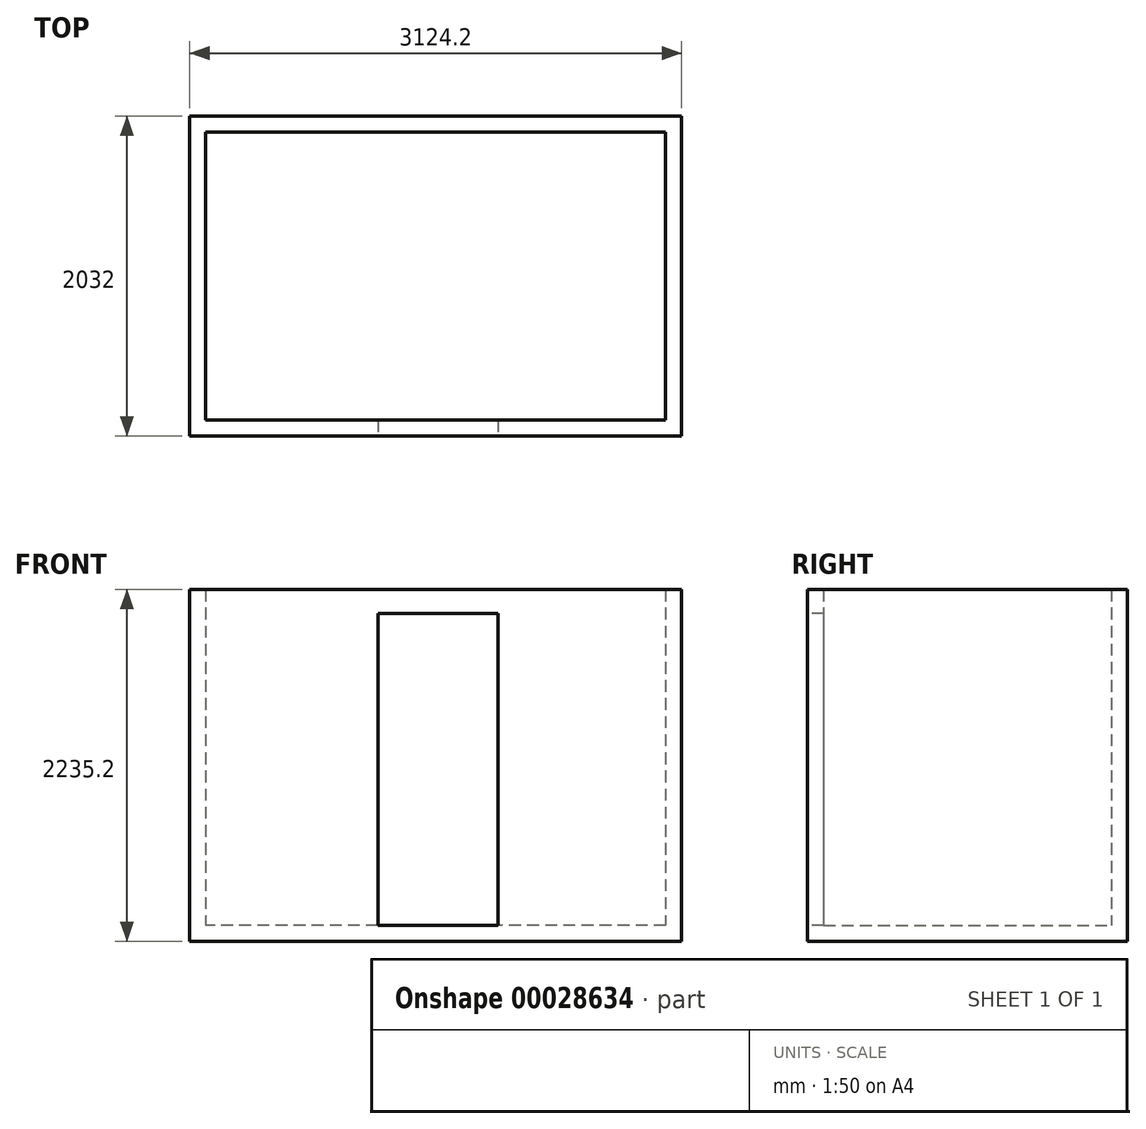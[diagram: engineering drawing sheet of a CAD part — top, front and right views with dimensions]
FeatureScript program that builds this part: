
annotation { "Feature Type Name" : "Feature", "Feature Type Description" : "" }
export const myFeature = defineFeature(function(context is Context, id is Id, definition is map)
    precondition{}
    {
        {
            var Q0;
            Q0=qCreatedBy(makeId("Top.planeOp"),FACE);
            var sketch = newSketch(context, id + "F0", { "sketchPlane" : qUnion([Q0])});
            skLineSegment(sketch, "E0.rect.bottom", {"start": v(1460.5, -914.4) * mm, "end": v(-1460.5, -914.4) * mm});
            skLineSegment(sketch, "E0.rect.top", {"start": v(1460.5, 914.4) * mm, "end": v(-1460.5, 914.4) * mm});
            skLineSegment(sketch, "E0.rect.left", {"start": v(1460.5, -914.4) * mm, "end": v(1460.5, 914.4) * mm});
            skLineSegment(sketch, "E0.rect.right", {"start": v(-1460.5, -914.4) * mm, "end": v(-1460.5, 914.4) * mm});
            skPoint(sketch, "E0.rect.middle", {"position": v(0, 0) * mm});
            skSolve(sketch);
        }
        {
            var Q0;
            Q0 = qSketchRegion(id + "F0", true);
            extrude(context, id + "F1", {"entities" : qUnion([Q0]), "depth" : 2133.6 * mm});
        }
        {
            var Q0;
            Q0=makeQuery(id+"F1.opExtrude","CAP_FACE",FACE,{"disambiguationData":[OSD([sQuery(id+"F0.wireOp",EDGE,"E0.rect.bottom"),sQuery(id+"F0.wireOp",EDGE,"E0.rect.top"),sQuery(id+"F0.wireOp",EDGE,"E0.rect.left"),sQuery(id+"F0.wireOp",EDGE,"E0.rect.right")])],"isStart":false});
            var Q1;
            Q1=makeQuery(id+"F1.opExtrude","SWEPT_BODY",BODY,{"disambiguationData":[OSD([sQuery(id+"F0.wireOp",EDGE,"E0.rect.bottom"),sQuery(id+"F0.wireOp",EDGE,"E0.rect.top"),sQuery(id+"F0.wireOp",EDGE,"E0.rect.left"),sQuery(id+"F0.wireOp",EDGE,"E0.rect.right")])]});
            shell(context, id + "F2", {"entities" : qUnion([Q0]), "parts" : qUnion([Q1]), "thickness" : 101.6 * mm, "oppositeDirection" : true});
        }
        {
            var Q0;
            Q0=makeQuery(id+"F1.opExtrude","SWEPT_FACE",FACE,{"disambiguationData":[OSD([sQuery(id+"F0.wireOp",EDGE,"E0.rect.bottom")])]});
            var sketch = newSketch(context, id + "F3", { "sketchPlane" : qUnion([Q0])});
            skLineSegment(sketch, "E1.bottom", {"start": v(-367.73, 0) * mm, "end": v(394.27, 0) * mm});
            skLineSegment(sketch, "E1.top", {"start": v(-367.73, 1981.2) * mm, "end": v(394.27, 1981.2) * mm});
            skLineSegment(sketch, "E1.left", {"start": v(-367.73, 0) * mm, "end": v(-367.73, 1981.2) * mm});
            skLineSegment(sketch, "E1.right", {"start": v(394.27, 0) * mm, "end": v(394.27, 1981.2) * mm});
            skSolve(sketch);
        }
        {
            var Q0;
            Q0 = qSketchRegion(id + "F3", true);
            extrude(context, id + "F4", {"entities" : qUnion([Q0]), "operationType" : NewBodyOperationType.REMOVE, "endBound" : BoundingType.UP_TO_NEXT, "oppositeDirection" : true, "depth" : 25.4 * mm});
        }
    });
